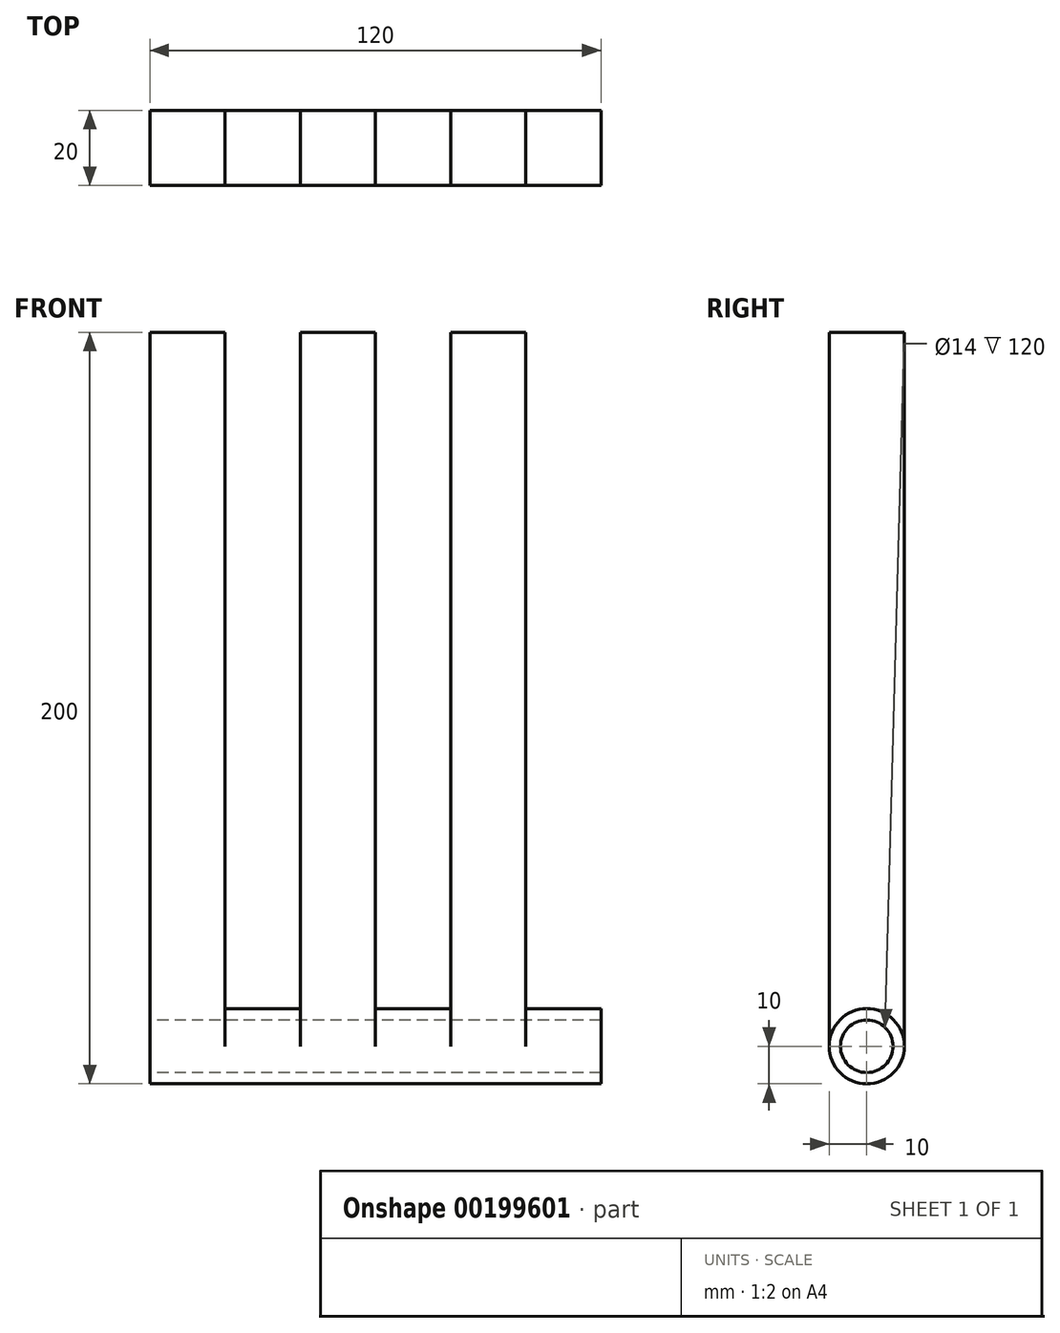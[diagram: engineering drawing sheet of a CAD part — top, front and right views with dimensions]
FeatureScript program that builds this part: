
annotation { "Feature Type Name" : "Feature", "Feature Type Description" : "" }
export const myFeature = defineFeature(function(context is Context, id is Id, definition is map)
    precondition{}
    {
        {
            assignVariable(context, id + "F0", {"name" : "width", "anyValue" : 120 * mm});
        }
        {
            var Q0;
            Q0=qCreatedBy(makeId("Front.planeOp"),FACE);
            var sketch = newSketch(context, id + "F1", { "sketchPlane" : qUnion([Q0])});
            skLineSegment(sketch, "E0.bottom", {"start": v(0, 0) * mm, "end": v(120, 0) * mm});
            skLineSegment(sketch, "E0.top", {"start": v(0, 200) * mm, "end": v(120, 200) * mm});
            skLineSegment(sketch, "E0.left", {"start": v(0, 0) * mm, "end": v(0, 200) * mm});
            skLineSegment(sketch, "E0.right", {"start": v(120, 0) * mm, "end": v(120, 200) * mm});
            skSolve(sketch);
        }
        {
            var Q0;
            Q0=qSketchRegion(id+"F1",true);
            extrude(context, id + "F2", {"entities" : qUnion([Q0]), "depth" : 1 / 6 * getVariable(context, 'width')});
        }
        {
            var Q0;
            Q0=makeQuery(id+"F2.opExtrude","SWEPT_FACE",FACE,{"disambiguationData":[OSD([sQuery(id+"F1.wireOp",EDGE,"E0.left")])]});
            var sketch = newSketch(context, id + "F3", { "sketchPlane" : qUnion([Q0])});
            skCircle(sketch, "E1", {"center": v(10, 10) * mm, "radius": 10 * mm});
            skPoint(sketch, "E1.centerSnap0", {"position": v(10, 0) * mm});
            skSolve(sketch);
        }
        {
            var Q0;
            {var subQ0=sQuery(id+"F3.wireOp",EDGE,"E1");var subQ1=sQuery(id+"F1.wireOp",EDGE,"E0.left");var subQ2=makeQuery(id+"F2.opExtrude","CAP_EDGE",EDGE,{"disambiguationData":[OSD([subQ1])],"isStart":false});var subQ3=makeQuery(id+"F3.imprint","INTERSECT",VERTEX,{"derivedFrom":[subQ2,subQ0]});Q0=makeQuery(id+"F3.imprint","IMPRINT",FACE,{"disambiguationData":[TD([[makeQuery(id+"F3.imprint","IMPRINT",EDGE,{"disambiguationData":[TD([[subQ3,1.0]])],"derivedFrom":subQ0}),-1.0]])]});}
            var Q1;
            {var subQ0=sQuery(id+"F3.wireOp",EDGE,"E1");var subQ1=sQuery(id+"F1.wireOp",EDGE,"E0.left");var subQ2=makeQuery(id+"F2.opExtrude","CAP_EDGE",EDGE,{"disambiguationData":[OSD([subQ1])],"isStart":true});var subQ3=makeQuery(id+"F3.imprint","INTERSECT",VERTEX,{"derivedFrom":[subQ2,subQ0]});Q1=makeQuery(id+"F3.imprint","IMPRINT",FACE,{"disambiguationData":[TD([[makeQuery(id+"F3.imprint","IMPRINT",EDGE,{"disambiguationData":[TD([[subQ3,-1.0]])],"derivedFrom":subQ0}),-1.0]])]});}
            var Q2;
            Q2=makeQuery(id+"F2.opExtrude","CAP_EDGE",EDGE,{"disambiguationData":[OSD([sQuery(id+"F1.wireOp",EDGE,"E0.bottom")])],"isStart":false});
            sweep(context, id + "F4", {"operationType" : NewBodyOperationType.REMOVE, "profiles" : qUnion([Q0, Q1]), "path" : qUnion([Q2])});
        }
        {
            var Q0;
            Q0=makeQuery(id+"F2.opExtrude","CAP_FACE",FACE,{"disambiguationData":[OSD([sQuery(id+"F1.wireOp",EDGE,"E0.bottom"),sQuery(id+"F1.wireOp",EDGE,"E0.top"),sQuery(id+"F1.wireOp",EDGE,"E0.left"),sQuery(id+"F1.wireOp",EDGE,"E0.right")])],"isStart":false});
            var sketch = newSketch(context, id + "F5", { "sketchPlane" : qUnion([Q0])});
            skLineSegment(sketch, "E2", {"start": v(60, 200) * mm, "end": v(60, 10) * mm});
            skLineSegment(sketch, "E3", {"start": v(20, 200) * mm, "end": v(20, 10) * mm});
            skLineSegment(sketch, "E4", {"start": v(40, 200) * mm, "end": v(40, 10) * mm});
            skLineSegment(sketch, "E5.MirrorCS", {"start": v(80, 200) * mm, "end": v(80, 10) * mm});
            skLineSegment(sketch, "E6.MirrorCS", {"start": v(100, 200) * mm, "end": v(100, 10) * mm});
            skSolve(sketch);
        }
        {
            var Q0;
            {var subQ0=sQuery(id+"F5.wireOp",EDGE,"E3");Q0=makeQuery(id+"F5.imprint","IMPRINT",FACE,{"disambiguationData":[TD([[makeQuery(id+"F5.imprint","IMPRINT",EDGE,{"derivedFrom":subQ0}),1.0]])]});}
            var Q1;
            {var subQ0=sQuery(id+"F5.wireOp",EDGE,"E2");Q1=makeQuery(id+"F5.imprint","IMPRINT",FACE,{"disambiguationData":[TD([[makeQuery(id+"F5.imprint","IMPRINT",EDGE,{"derivedFrom":subQ0}),1.0]])]});}
            var Q2;
            {var subQ0=sQuery(id+"F5.wireOp",EDGE,"E6.MirrorCS");Q2=makeQuery(id+"F5.imprint","IMPRINT",FACE,{"disambiguationData":[TD([[makeQuery(id+"F5.imprint","IMPRINT",EDGE,{"derivedFrom":subQ0}),1.0]])]});}
            var Q3;
            Q3=qConstructionFilter(qBodyType(qCreatedBy(id+"F3",EDGE),BodyType.WIRE),ConstructionObject.NO);
            sweep(context, id + "F6", {"operationType" : NewBodyOperationType.REMOVE, "profiles" : qUnion([Q0, Q1, Q2]), "path" : qUnion([Q3])});
        }
        {
            var Q0;
            Q0=makeQuery(id+"F2.opExtrude","SWEPT_FACE",FACE,{"disambiguationData":[OSD([sQuery(id+"F1.wireOp",EDGE,"E0.left")])]});
            var sketch = newSketch(context, id + "F7", { "sketchPlane" : qUnion([Q0])});
            skCircle(sketch, "E7", {"center": v(10, 10) * mm, "radius": 7 * mm});
            skSolve(sketch);
        }
        {
            var Q0;
            Q0=qSketchRegion(id+"F7",true);
            extrude(context, id + "F8", {"entities" : qUnion([Q0]), "operationType" : NewBodyOperationType.REMOVE, "endBound" : BoundingType.THROUGH_ALL, "oppositeDirection" : true, "depth" : 25 * mm});
        }
    });
